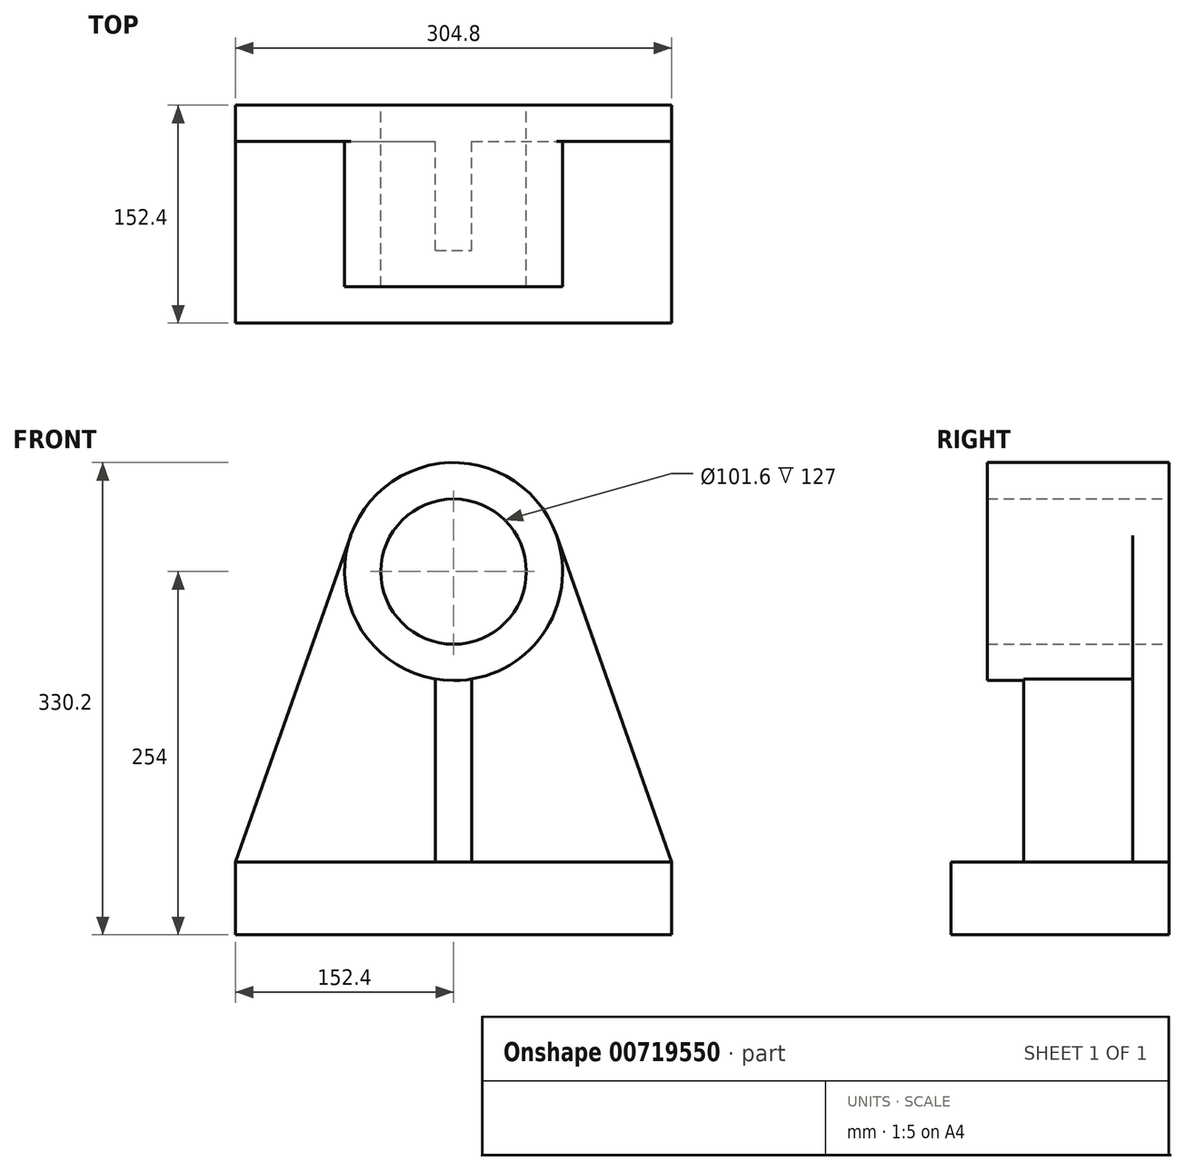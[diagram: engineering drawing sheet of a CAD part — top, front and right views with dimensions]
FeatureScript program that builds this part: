
annotation { "Feature Type Name" : "Feature", "Feature Type Description" : "" }
export const myFeature = defineFeature(function(context is Context, id is Id, definition is map)
    precondition{}
    {
        {
            var Q0;
            Q0=qCreatedBy(makeId("Front.planeOp"),FACE);
            var sketch = newSketch(context, id + "F0", { "sketchPlane" : qUnion([Q0])});
            skCircle(sketch, "E0", {"center": v(0, 0) * mm, "radius": 50.8 * mm});
            skCircle(sketch, "E1", {"center": v(0, 0) * mm, "radius": 76.2 * mm});
            skSolve(sketch);
        }
        {
            var Q0;
            Q0=makeQuery(id+"F0.imprint","IMPRINT",FACE,{"disambiguationData":[TD([[makeQuery(id+"F0.imprint","IMPRINT",EDGE,{"derivedFrom":sQuery(id+"F0.wireOp",EDGE,"E0")}),-1.0]])]});
            extrude(context, id + "F1", {"entities" : qUnion([Q0]), "depth" : 127 * mm, "offsetDistance" : 25.4 * mm});
        }
        {
            var Q0;
            Q0=qCreatedBy(makeId("Front.planeOp"),FACE);
            var sketch = newSketch(context, id + "F2", { "sketchPlane" : qUnion([Q0])});
            skCircle(sketch, "E2", {"center": v(0, 0) * mm, "radius": 76.2 * mm});
            skLineSegment(sketch, "E3", {"start": v(-71.87, 25.33) * mm, "end": v(-152.4, -203.2) * mm});
            skLineSegment(sketch, "E4", {"start": v(71.87, 25.33) * mm, "end": v(152.4, -203.2) * mm});
            skLineSegment(sketch, "E5", {"start": v(-152.4, -203.2) * mm, "end": v(152.4, -203.2) * mm});
            skSolve(sketch);
        }
        {
            var Q0;
            {var subQ0=sQuery(id+"F2.wireOp",EDGE,"E3");Q0=makeQuery(id+"F2.imprint","IMPRINT",FACE,{"disambiguationData":[TD([[makeQuery(id+"F2.imprint","IMPRINT",EDGE,{"derivedFrom":subQ0}),1.0]])]});}
            extrude(context, id + "F3", {"entities" : qUnion([Q0]), "operationType" : NewBodyOperationType.ADD, "depth" : 25.4 * mm, "offsetDistance" : 25.4 * mm});
        }
        {
            var Q0;
            Q0=qCreatedBy(makeId("Front.planeOp"),FACE);
            var sketch = newSketch(context, id + "F4", { "sketchPlane" : qUnion([Q0])});
            skLineSegment(sketch, "E6", {"start": v(-152.4, -203.2) * mm, "end": v(152.4, -203.2) * mm});
            skLineSegment(sketch, "E7", {"start": v(152.4, -203.2) * mm, "end": v(152.4, -254) * mm});
            skLineSegment(sketch, "E8", {"start": v(152.4, -254) * mm, "end": v(-152.4, -254) * mm});
            skLineSegment(sketch, "E9", {"start": v(-152.4, -254) * mm, "end": v(-152.4, -203.2) * mm});
            skSolve(sketch);
        }
        {
            var Q0;
            Q0=makeQuery(id+"F4.imprint","IMPRINT",FACE,{"disambiguationData":[TD([[makeQuery(id+"F4.imprint","IMPRINT",EDGE,{"derivedFrom":sQuery(id+"F4.wireOp",EDGE,"E6")}),-1.0]])]});
            extrude(context, id + "F5", {"entities" : qUnion([Q0]), "operationType" : NewBodyOperationType.ADD, "depth" : 152.4 * mm, "offsetDistance" : 25.4 * mm});
        }
        {
            var Q0;
            Q0=makeQuery(id+"F3.opExtrude","CAP_FACE",FACE,{"disambiguationData":[OSD([sQuery(id+"F2.wireOp",EDGE,"E2"),sQuery(id+"F2.wireOp",EDGE,"E3"),sQuery(id+"F2.wireOp",EDGE,"E4"),sQuery(id+"F2.wireOp",EDGE,"E5")])],"isStart":false});
            var sketch = newSketch(context, id + "F6", { "sketchPlane" : qUnion([Q0])});
            skLineSegment(sketch, "E10", {"start": v(-12.7, -203.2) * mm, "end": v(12.7, -203.2) * mm});
            skLineSegment(sketch, "E11", {"start": v(12.7, -203.2) * mm, "end": v(12.7, -75.13) * mm});
            skLineSegment(sketch, "E12", {"start": v(-12.7, -203.2) * mm, "end": v(-12.7, -75.13) * mm});
            skCircle(sketch, "E13", {"center": v(0, 0) * mm, "radius": 76.2 * mm});
            skSolve(sketch);
        }
        {
            var Q0;
            Q0=makeQuery(id+"F6.imprint","IMPRINT",FACE,{"disambiguationData":[TD([[makeQuery(id+"F6.imprint","IMPRINT",EDGE,{"derivedFrom":sQuery(id+"F6.wireOp",EDGE,"E10")}),1.0]])]});
            extrude(context, id + "F7", {"entities" : qUnion([Q0]), "operationType" : NewBodyOperationType.ADD, "depth" : 76.2 * mm, "offsetDistance" : 25.4 * mm});
        }
        {
            var Q0;
            Q0=makeQuery(id+"F1.opExtrude","SWEPT_BODY",BODY,{"disambiguationData":[OSD([sQuery(id+"F0.wireOp",EDGE,"E0"),sQuery(id+"F0.wireOp",EDGE,"E1")])]});
            transform(context, id + "F8", {"entities" : qUnion([Q0]), "transformType" : TransformType.TRANSLATION_3D, "dx" : 0 * mm, "dy" : 0 * mm, "dz" : 0 * mm, "makeCopy" : true});
        }
        {
            var Q0;
            Q0=makeQuery(id+"F8.opPattern","COPY",BODY,{"derivedFrom":makeQuery(id+"F1.opExtrude","SWEPT_BODY",BODY,{"disambiguationData":[OSD([sQuery(id+"F0.wireOp",EDGE,"E0"),sQuery(id+"F0.wireOp",EDGE,"E1")])]}),"instanceName":"1"});
            deleteBodies(context, id + "F9", {"entities" : qUnion([Q0])});
        }
    });
